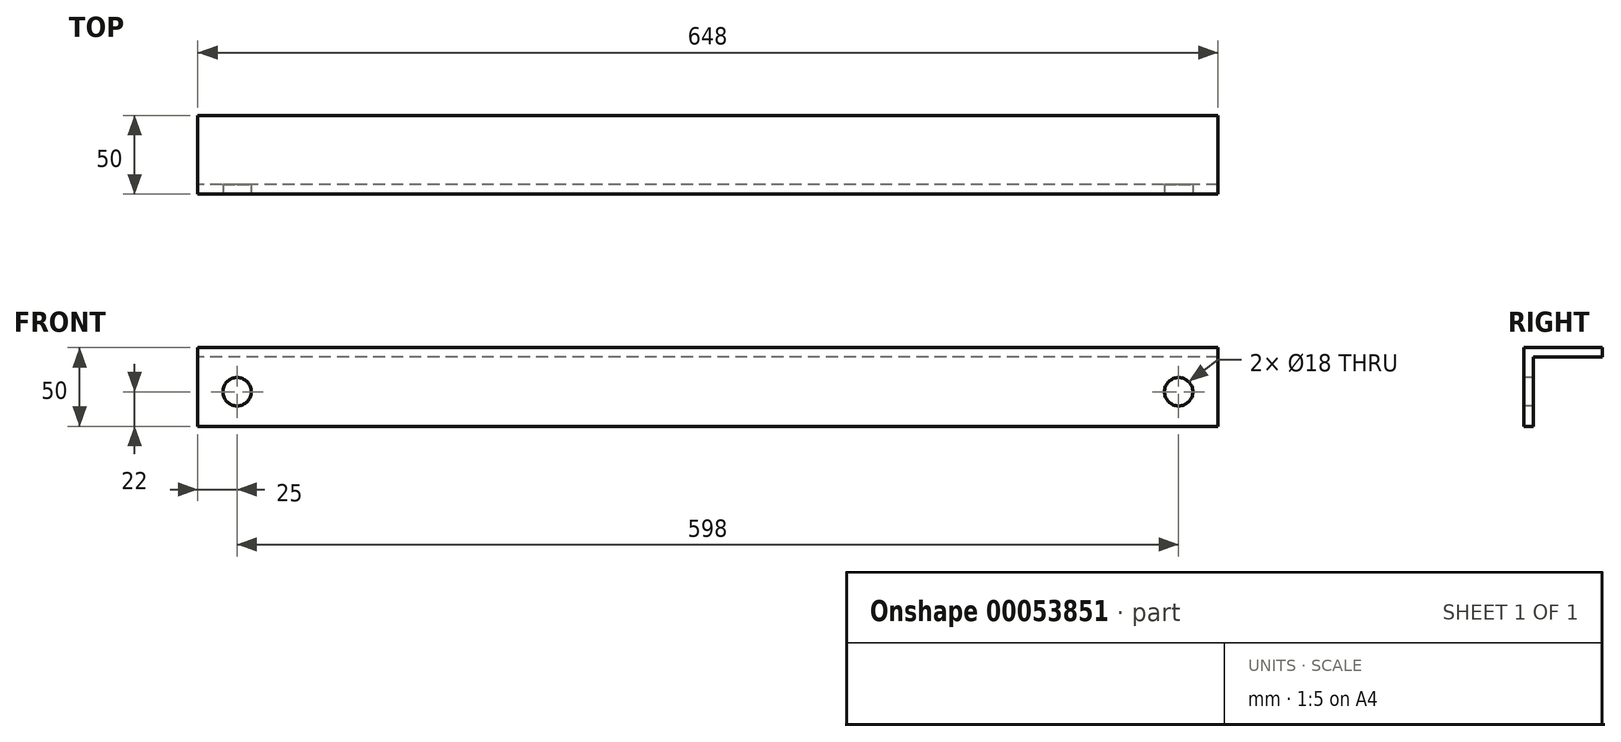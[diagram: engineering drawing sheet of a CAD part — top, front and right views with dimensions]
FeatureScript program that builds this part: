
annotation { "Feature Type Name" : "Feature", "Feature Type Description" : "" }
export const myFeature = defineFeature(function(context is Context, id is Id, definition is map)
    precondition{}
    {
        {
            var Q0;
            Q0=qCreatedBy(makeId("Front.planeOp"),FACE);
            var sketch = newSketch(context, id + "F0", { "sketchPlane" : qUnion([Q0])});
            skLineSegment(sketch, "E0.bottom", {"start": v(0, 0) * mm, "end": v(648, 0) * mm});
            skLineSegment(sketch, "E0.top", {"start": v(0, 50) * mm, "end": v(648, 50) * mm});
            skLineSegment(sketch, "E0.left", {"start": v(0, 0) * mm, "end": v(0, 50) * mm});
            skLineSegment(sketch, "E0.right", {"start": v(648, 0) * mm, "end": v(648, 50) * mm});
            skSolve(sketch);
        }
        {
            var Q0;
            Q0 = qSketchRegion(id + "F0", true);
            extrude(context, id + "F1", {"entities" : qUnion([Q0]), "depth" : 6 * mm});
        }
        {
            var Q0;
            Q0=makeQuery(id+"F1.opExtrude","CAP_FACE",FACE,{"disambiguationData":[OSD([sQuery(id+"F0.wireOp",EDGE,"E0.bottom"),sQuery(id+"F0.wireOp",EDGE,"E0.top"),sQuery(id+"F0.wireOp",EDGE,"E0.left"),sQuery(id+"F0.wireOp",EDGE,"E0.right")])],"isStart":true});
            var sketch = newSketch(context, id + "F2", { "sketchPlane" : qUnion([Q0])});
            skLineSegment(sketch, "E1.bottom", {"start": v(-648, 50) * mm, "end": v(0, 50) * mm});
            skLineSegment(sketch, "E1.top", {"start": v(-648, 44) * mm, "end": v(0, 44) * mm});
            skLineSegment(sketch, "E1.left", {"start": v(-648, 50) * mm, "end": v(-648, 44) * mm});
            skLineSegment(sketch, "E1.right", {"start": v(0, 50) * mm, "end": v(0, 44) * mm});
            skSolve(sketch);
        }
        {
            var Q0;
            Q0 = qSketchRegion(id + "F2", true);
            extrude(context, id + "F3", {"entities" : qUnion([Q0]), "operationType" : NewBodyOperationType.ADD, "depth" : 44 * mm});
        }
        {
            var Q0;
            Q0=makeQuery(id+"F1.opExtrude","CAP_FACE",FACE,{"disambiguationData":[OSD([sQuery(id+"F0.wireOp",EDGE,"E0.bottom"),sQuery(id+"F0.wireOp",EDGE,"E0.top"),sQuery(id+"F0.wireOp",EDGE,"E0.left"),sQuery(id+"F0.wireOp",EDGE,"E0.right")])],"isStart":false});
            var sketch = newSketch(context, id + "F4", { "sketchPlane" : qUnion([Q0])});
            skCircle(sketch, "E2", {"center": v(25, 22) * mm, "radius": 9 * mm});
            skCircle(sketch, "E3", {"center": v(623, 22) * mm, "radius": 9 * mm});
            skSolve(sketch);
        }
        {
            var Q0;
            Q0 = qSketchRegion(id + "F4", true);
            extrude(context, id + "F5", {"entities" : qUnion([Q0]), "operationType" : NewBodyOperationType.REMOVE, "endBound" : BoundingType.THROUGH_ALL, "oppositeDirection" : true, "depth" : 25 * mm});
        }
    });
